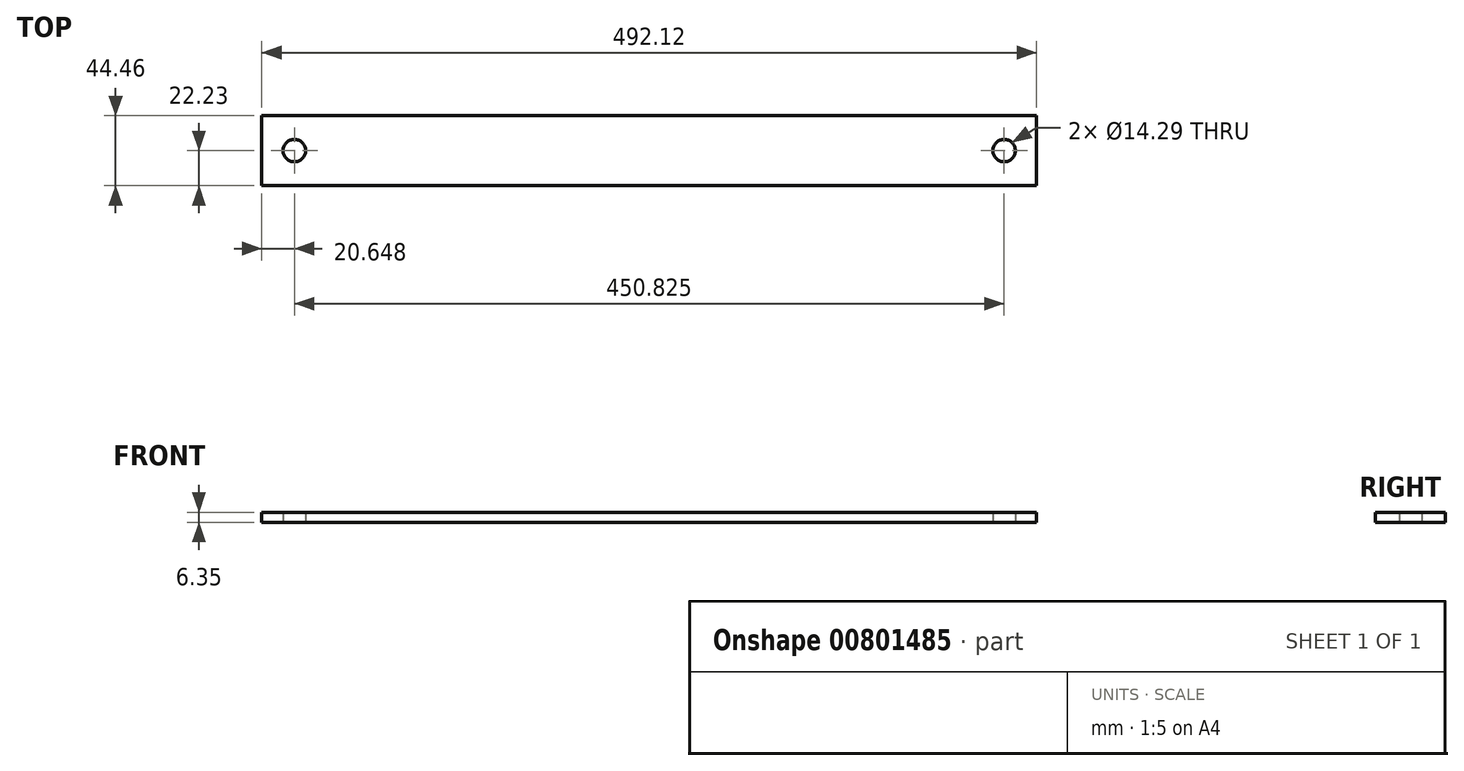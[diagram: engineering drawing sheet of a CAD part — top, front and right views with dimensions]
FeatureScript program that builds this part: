
annotation { "Feature Type Name" : "Feature", "Feature Type Description" : "" }
export const myFeature = defineFeature(function(context is Context, id is Id, definition is map)
    precondition{}
    {
        {
            var Q0;
            Q0=qCreatedBy(makeId("Top.planeOp"),FACE);
            var sketch = newSketch(context, id + "F0", { "sketchPlane" : qUnion([Q0])});
            skLineSegment(sketch, "E0.bottom", {"start": v(246.06, -22.22) * mm, "end": v(-246.06, -22.23) * mm});
            skLineSegment(sketch, "E0.top", {"start": v(246.06, 22.23) * mm, "end": v(-246.06, 22.22) * mm});
            skLineSegment(sketch, "E0.left", {"start": v(246.06, -22.22) * mm, "end": v(246.06, 22.23) * mm});
            skLineSegment(sketch, "E0.right", {"start": v(-246.06, -22.23) * mm, "end": v(-246.06, 22.22) * mm});
            skPoint(sketch, "E0.middle", {"position": v(0, 0) * mm});
            skCircle(sketch, "E1", {"center": v(-225.41, 0) * mm, "radius": 7.14 * mm});
            skCircle(sketch, "E2.MirrorC", {"center": v(225.41, 0) * mm, "radius": 7.14 * mm});
            skSolve(sketch);
        }
        {
            var Q0;
            Q0 = qSketchRegion(id + "F0", true);
            extrude(context, id + "F1", {"entities" : qUnion([Q0]), "depth" : 6.35 * mm, "offsetDistance" : 25.4 * mm});
        }
    });
